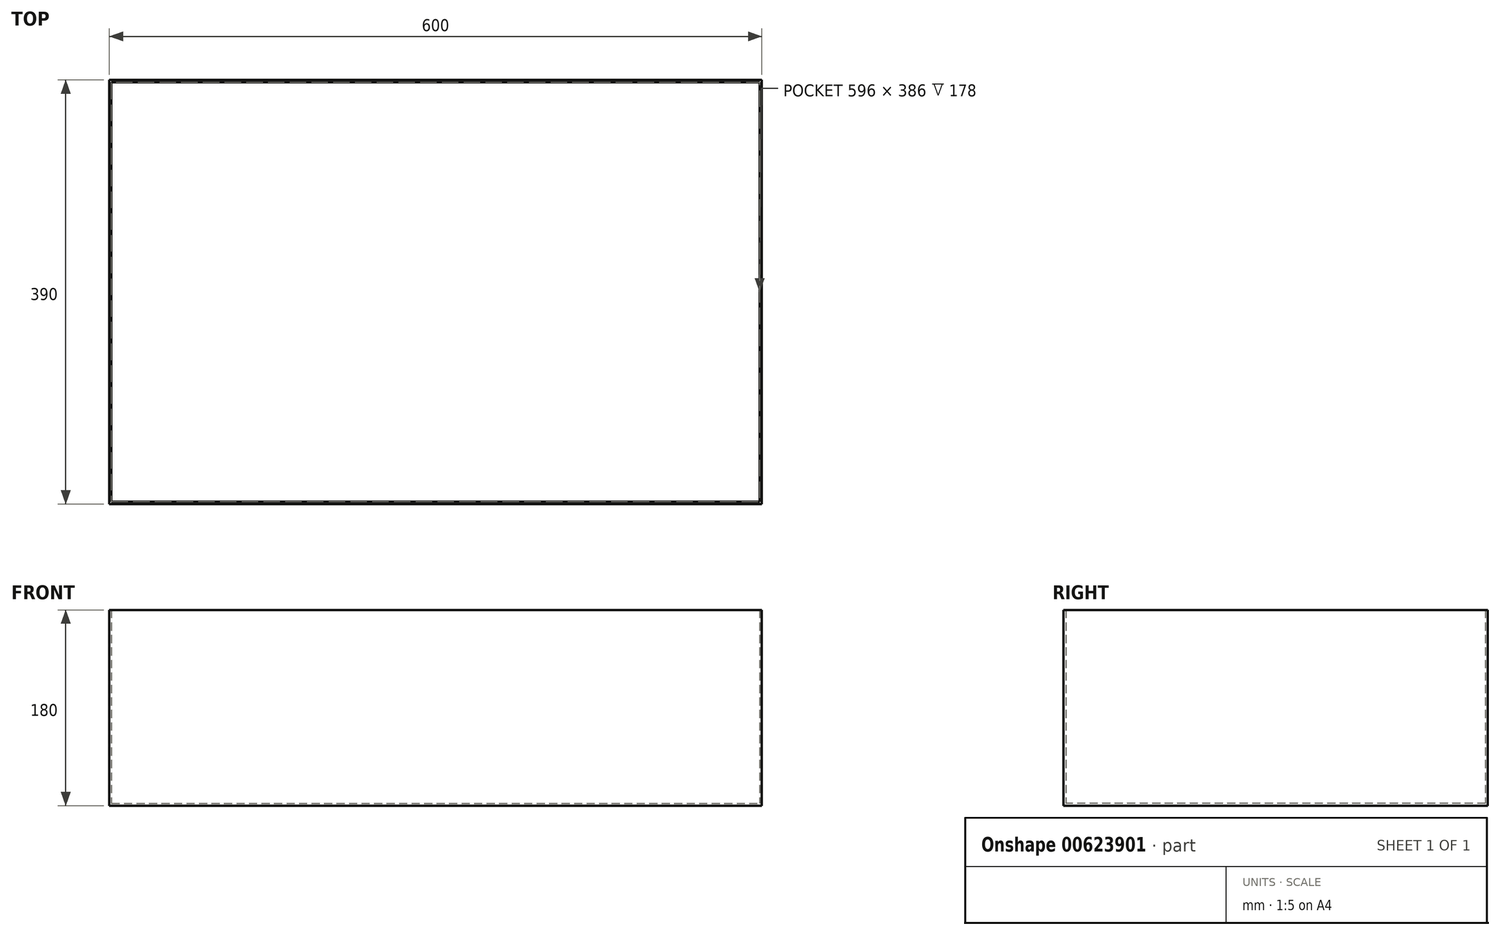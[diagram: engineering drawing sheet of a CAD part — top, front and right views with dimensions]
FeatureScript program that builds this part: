
annotation { "Feature Type Name" : "Feature", "Feature Type Description" : "" }
export const myFeature = defineFeature(function(context is Context, id is Id, definition is map)
    precondition{}
    {
        {
            var Q0;
            Q0=qCreatedBy(makeId("Top.planeOp"),FACE);
            var sketch = newSketch(context, id + "F0", { "sketchPlane" : qUnion([Q0])});
            skLineSegment(sketch, "E0.bottom", {"start": v(0, 0) * mm, "end": v(600, 0) * mm});
            skLineSegment(sketch, "E0.top", {"start": v(0, -390) * mm, "end": v(600, -390) * mm});
            skLineSegment(sketch, "E0.left", {"start": v(0, 0) * mm, "end": v(0, -390) * mm});
            skLineSegment(sketch, "E0.right", {"start": v(600, 0) * mm, "end": v(600, -390) * mm});
            skSolve(sketch);
        }
        {
            var Q0;
            Q0 = qSketchRegion(id + "F0", true);
            extrude(context, id + "F1", {"entities" : qUnion([Q0]), "depth" : 2 * mm, "offsetDistance" : 25 * mm});
        }
        {
            var Q0;
            Q0=makeQuery(id+"F1.opExtrude","CAP_FACE",FACE,{"disambiguationData":[OSD([sQuery(id+"F0.wireOp",EDGE,"E0.bottom"),sQuery(id+"F0.wireOp",EDGE,"E0.top"),sQuery(id+"F0.wireOp",EDGE,"E0.left"),sQuery(id+"F0.wireOp",EDGE,"E0.right")])],"isStart":false});
            var sketch = newSketch(context, id + "F2", { "sketchPlane" : qUnion([Q0])});
            skLineSegment(sketch, "E1.bottom", {"start": v(2, -2) * mm, "end": v(598, -2) * mm});
            skLineSegment(sketch, "E1.top", {"start": v(2, -388) * mm, "end": v(598, -388) * mm});
            skLineSegment(sketch, "E1.left", {"start": v(2, -2) * mm, "end": v(2, -388) * mm});
            skLineSegment(sketch, "E1.right", {"start": v(598, -2) * mm, "end": v(598, -388) * mm});
            skSolve(sketch);
        }
        {
            var Q0;
            Q0=makeQuery(id+"F2.imprint","IMPRINT",FACE,{"disambiguationData":[TD([[makeQuery(id+"F2.imprint","IMPRINT",EDGE,{"derivedFrom":sQuery(id+"F2.wireOp",EDGE,"E1.bottom")}),1.0]])]});
            extrude(context, id + "F3", {"entities" : qUnion([Q0]), "operationType" : NewBodyOperationType.ADD, "depth" : 178 * mm, "offsetDistance" : 25 * mm});
        }
    });
